# Revit family: AR100G
name_source: partatom
category: Modelos genéricos
revit_build: Autodesk Revit 2017 (Build: 20181011_1645(x64)
units: mm (PartAtom-declared; Revit-internal decimal feet)

## family parameters
Compartido = No
Corte con vacíos al cargar = No
Cota de conector redondo = Diámetro de uso
Puede alojar armadura = No
Punto de cálculo de habitación = No
Se basa en plano de trabajo = No
Siempre vertical = Sí
Tipo de pieza = Normal

## types (1)
- AR100G
    Altura = 490 mm  [stored 1.60761 ft]
    Anchura exterior = 136 mm
    Anchura interior = 100 mm  [stored 0.328084 ft]
    Clase de carga = D-400 Norma EN-1433
    Costo = 130.14 $
    Descripción = Arqueta de Hormigón Polímero tipo ULMA para recogida de aguas pluviales.
    Diseño = 1 cuerpo
    Fabricante = ULMA Architectural
    Ficha técnica = http://www.ulmaarchitectural.com
    Longitud = 500 mm  [stored 1.64042 ft]
    Modelo = AR100G
    Peso = 0.00 kg
    Serie canales = MultiV+ R100G
    URL = http://www.ulmaarchitectural.com
    Ø salida frontal = 90 mm
    Ø salida lateral = 160 mm

note: [stored X ft] marks values corroborated as IEEE doubles in the binary element streams (Revit-internal decimal feet)
